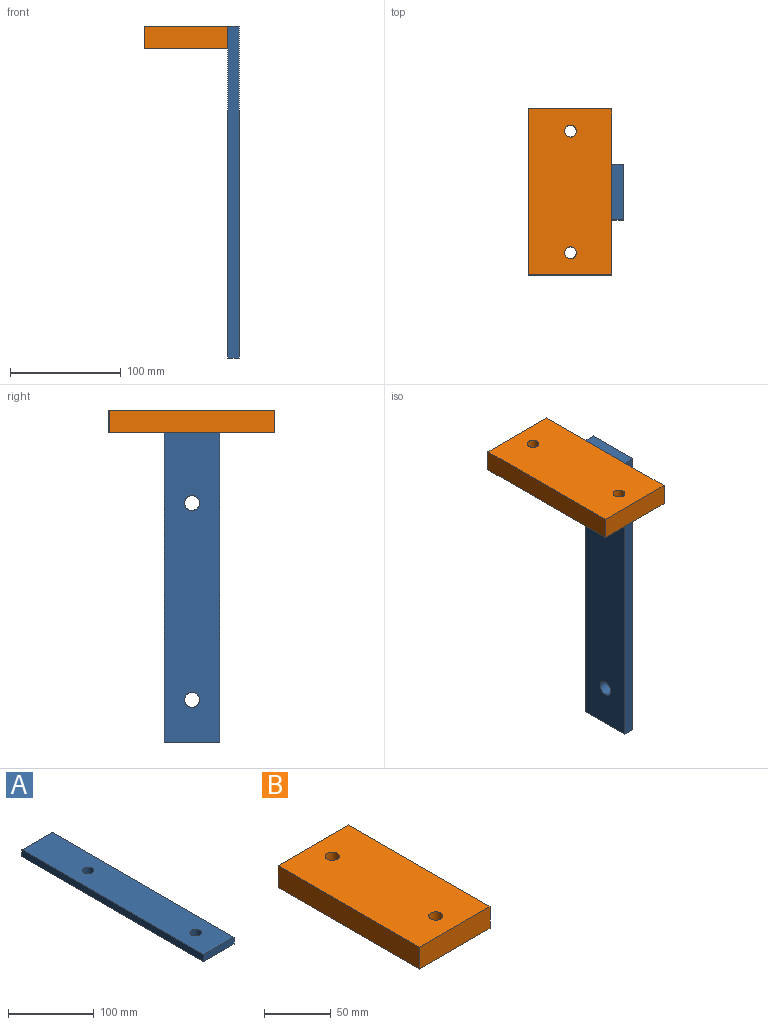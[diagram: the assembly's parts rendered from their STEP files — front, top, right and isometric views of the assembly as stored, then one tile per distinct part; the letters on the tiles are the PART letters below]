
ASSEMBLY  parts=2 mates=1
PART A: 8 faces, bbox 50x300x10 mm
  f0: plane 50x10mm, normal (0,-1,0), area 500mm2, adj f1,f3,f4,f5
  f1: plane 300x10mm, normal (1,0,0), area 3000mm2, adj f0,f2,f4,f5
  f2: plane 50x10mm, normal (0,1,0), area 500mm2, adj f1,f3,f4,f5
  f3: plane 300x10mm, normal (-1,0,0), area 3000mm2, adj f0,f2,f4,f5
  f4: plane 300x50mm, normal (0,0,1), area 14713.7mm2, adj f0,f1,f2,f3,f6,f7
  f5: plane 300x50mm, normal (0,0,-1), area 14713.7mm2, adj f0,f1,f2,f3,f6,f7
  f6: cylinder r=6.75mm len=13.5mm, axis (0,0,1), area 424.1mm2, adj f4,f5
  f7: cylinder r=6.75mm len=13.5mm, axis (0,0,1), area 424.1mm2, adj f4,f5
PART B: 8 faces, bbox 75x150x20 mm
  f0: plane 75x20mm, normal (0,-1,0), area 1500mm2, adj f1,f3,f4,f5
  f1: plane 150x20mm, normal (1,0,0), area 3000mm2, adj f0,f2,f4,f5
  f2: plane 75x20mm, normal (0,1,0), area 1500mm2, adj f1,f3,f4,f5
  f3: plane 150x20mm, normal (-1,0,0), area 3000mm2, adj f0,f2,f4,f5
  f4: plane 150x75mm, normal (0,0,1), area 11069.6mm2, adj f0,f1,f2,f3,f6,f7
  f5: plane 150x75mm, normal (0,0,-1), area 11069.6mm2, adj f0,f1,f2,f3,f6,f7
  f6: cylinder r=5.36mm len=20mm, axis (0,0,1), area 673.3mm2, adj f4,f5
  f7: cylinder r=5.36mm len=20mm, axis (0,0,1), area 673.3mm2, adj f4,f5
PLACE A rot(axis=(0.58,0.58,0.58),120deg) t=(39.05,-1.7,-129.85)mm
PLACE B t=(1.55,-1.7,0.15)mm
MATE fastened B.f1 <-> A.f5  axis (1,0,0) through (39.05,-1.7,20.15)mm
